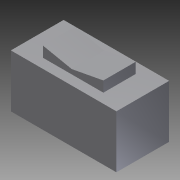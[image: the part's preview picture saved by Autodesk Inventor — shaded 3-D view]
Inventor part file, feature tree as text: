
AUTODESK INVENTOR PART (.ipt)
format: ipt  version: 2012 (Build 160160000, 160)  size: 84,992 bytes
history: native  units: in
note: dims shown in document units (in); Inventor stores cm internally (conversion verified against a paired STEP export)
features: extrude x3, sketch x3
ambient origin geometry x8: Origin, YZ Plane, XZ Plane, XY Plane, X Axis, Y Axis, Z Axis, Center Point
bodies: Solid1 (feature_tree)
feature tree (6):
  extrude  "Extrusion1"  Depth=0.5in
  extrude  "Extrusion2"  Depth=0.1in TaperAngle=0.0deg
  extrude  "Extrusion3"  [1 undecoded]
  sketch  "Sketch1"  dims[d0=1.0in d1=0.5in]
  sketch  "Sketch2"  dims[d2=0.5in d3=0.0in d4=0.1in d5=0.0in]
  sketch  "Sketch3"  dims[d6=2.0in d7=0.0in]
note: 1 required parameter value undecoded (feature->parameter linkage not recoverable at this tier; creation-order binding heuristic only, values carry confidence <= 0.55)
